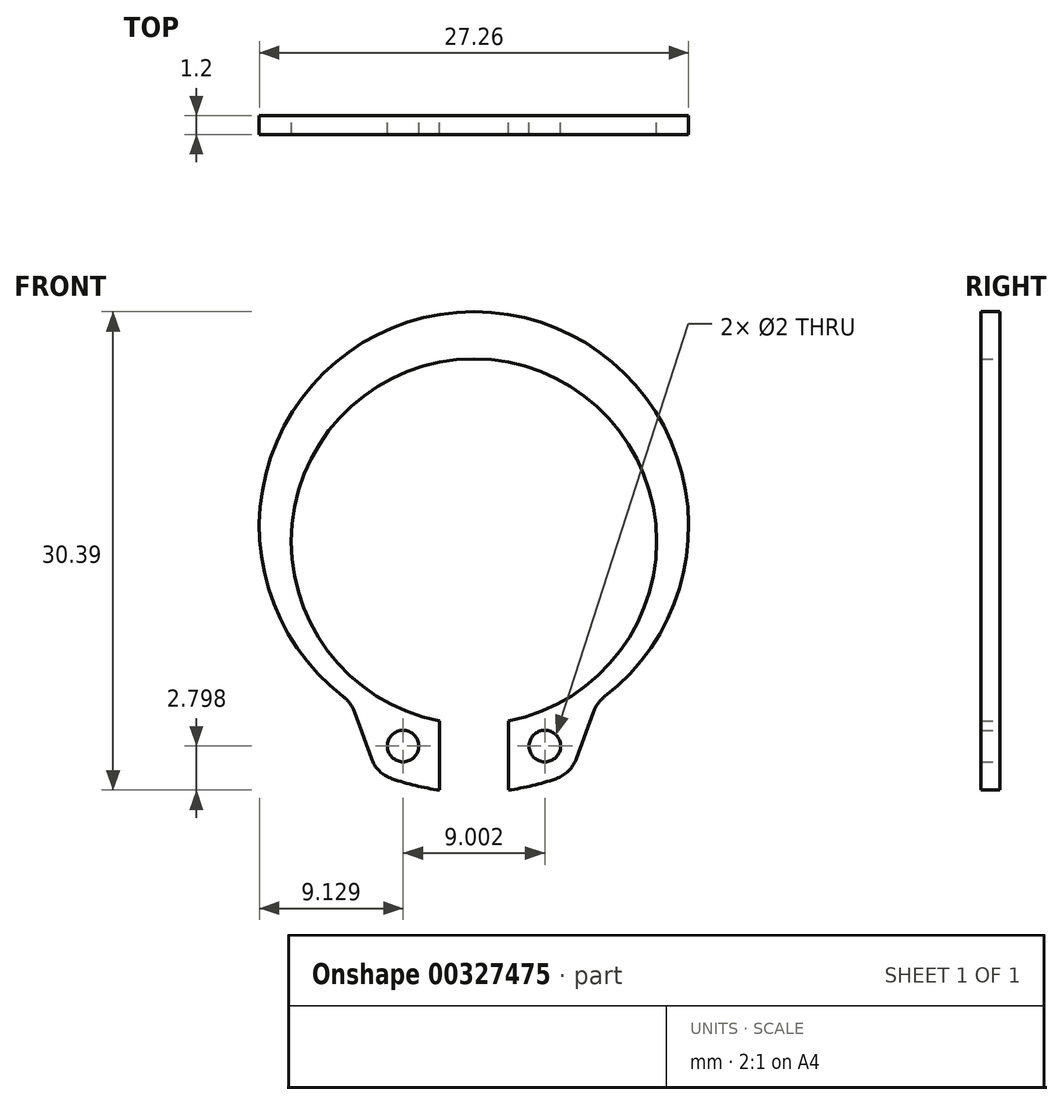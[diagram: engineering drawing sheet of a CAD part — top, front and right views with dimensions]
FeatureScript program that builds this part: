
annotation { "Feature Type Name" : "Feature", "Feature Type Description" : "" }
export const myFeature = defineFeature(function(context is Context, id is Id, definition is map)
    precondition{}
    {
        {
            var Q0;
            Q0=qCreatedBy(makeId("Front.planeOp"),FACE);
            var sketch = newSketch(context, id + "F0", { "sketchPlane" : qUnion([Q0])});
            skCircle(sketch, "E0", {"center": v(0, 0) * mm, "radius": 17.1 * mm, "construction": true});
            skArc(sketch, "E1", {"start": v(2.2, -11.39) * mm, "mid": v(0, 11.6) * mm, "end": v(-2.2, -11.39) * mm});
            skLineSegment(sketch, "E2", {"start": v(2.2, -11.39) * mm, "end": v(2.2, -15.79) * mm});
            skLineSegment(sketch, "E3", {"start": v(0, 0) * mm, "end": v(0, 16.86) * mm, "construction": true});
            skLineSegment(sketch, "E4", {"start": v(-2.2, -11.39) * mm, "end": v(-2.2, -15.79) * mm});
            skLineSegment(sketch, "E5", {"start": v(-2.2, -11.39) * mm, "end": v(0, -11.39) * mm, "construction": true});
            skCircle(sketch, "E6", {"center": v(-4.5, -13) * mm, "radius": 1 * mm});
            skCircle(sketch, "E7", {"center": v(4.5, -13) * mm, "radius": 1 * mm});
            skPoint(sketch, "E8", {"position": v(-2.2, -12.49) * mm});
            skArc(sketch, "E9", {"start": v(2.2, -12.49) * mm, "mid": v(0, 14.6) * mm, "end": v(-2.2, -12.49) * mm});
            skLineSegment(sketch, "E10", {"start": v(0, -11.39) * mm, "end": v(2.2, -11.39) * mm, "construction": true});
            skLineSegment(sketch, "E11", {"start": v(0, 0) * mm, "end": v(-11.6, 0) * mm, "construction": true});
            skLineSegment(sketch, "E12", {"start": v(0, 0) * mm, "end": v(11.6, 0) * mm, "construction": true});
            skLineSegment(sketch, "E13", {"start": v(11.6, 0) * mm, "end": v(13.6, 0) * mm, "construction": true});
            skLineSegment(sketch, "E14", {"start": v(-11.6, 0) * mm, "end": v(-13.6, 0) * mm, "construction": true});
            skArc(sketch, "E15", {"start": v(2.2, -15.79) * mm, "mid": v(4.23, -15.37) * mm, "end": v(6.18, -14.7) * mm});
            skLineSegment(sketch, "E16", {"start": v(-4.5, -13) * mm, "end": v(-4.5, -10.7) * mm, "construction": true});
            skLineSegment(sketch, "E17", {"start": v(-4.5, -13) * mm, "end": v(-4.5, -15.3) * mm, "construction": true});
            skLineSegment(sketch, "E18", {"start": v(4.5, -13) * mm, "end": v(4.5, -10.7) * mm, "construction": true});
            skLineSegment(sketch, "E19", {"start": v(4.5, -13) * mm, "end": v(4.5, -15.3) * mm, "construction": true});
            skLineSegment(sketch, "E20", {"start": v(-4.5, -13) * mm, "end": v(-2.2, -13) * mm, "construction": true});
            skLineSegment(sketch, "E21", {"start": v(4.5, -13) * mm, "end": v(2.2, -13) * mm, "construction": true});
            skLineSegment(sketch, "E22", {"start": v(-6.18, -14.7) * mm, "end": v(-7.82, -10.2) * mm});
            skLineSegment(sketch, "E23.MirrorCS", {"start": v(6.18, -14.7) * mm, "end": v(7.82, -10.2) * mm});
            skLineSegment(sketch, "E24", {"start": v(-4.5, -13) * mm, "end": v(-6.8, -13) * mm, "construction": true});
            skArc(sketch, "E25.trimOffspring", {"start": v(-6.18, -14.7) * mm, "mid": v(-4.23, -15.37) * mm, "end": v(-2.2, -15.79) * mm});
            skCircle(sketch, "E26", {"center": v(0, 0) * mm, "radius": 12.5 * mm, "construction": true});
            skSolve(sketch);
        }
        {
            var Q0;
            Q0=qSketchRegion(id+"F0",true);
            extrude(context, id + "F1", {"entities" : qUnion([Q0]), "depth" : 1.2 * mm});
        }
        {
            var Q0;
            Q0=makeQuery(id+"F1.opExtrude","SWEPT_EDGE",EDGE,{"disambiguationData":[OSD([sQuery(id+"F0.wireOp",EDGE,"907c1e65-be0d-4d4d-923e-d7fc0afcae600.MirrorCS"),sQuery(id+"F0.wireOp",EDGE,"ea3ce9a1-426e-48f8-a769-742e162fd32d0.MirrorCS")])]});
            var Q1;
            Q1=makeQuery(id+"F1.opExtrude","SWEPT_EDGE",EDGE,{"disambiguationData":[OSD([sQuery(id+"F0.wireOp",EDGE,"yB3Dk9i2-sZMU-oLhI-pwqJ-xhCv1nncbOm0"),sQuery(id+"F0.wireOp",EDGE,"pRWJiajO-2Cuv-CeR1-zJug-2Vsa7C0coXul")])]});
            var Q2;
            Q2=makeQuery(id+"F1.opExtrude","SWEPT_EDGE",EDGE,{"disambiguationData":[OSD([sQuery(id+"F0.wireOp",EDGE,"E15"),sQuery(id+"F0.wireOp",EDGE,"E23.MirrorCS")])]});
            var Q3;
            Q3=makeQuery(id+"F1.opExtrude","SWEPT_EDGE",EDGE,{"disambiguationData":[OSD([sQuery(id+"F0.wireOp",EDGE,"E22"),sQuery(id+"F0.wireOp",EDGE,"E25.trimOffspring")])]});
            var Q4;
            Q4=makeQuery(id+"F1.opExtrude","SWEPT_EDGE",EDGE,{"disambiguationData":[OSD([sQuery(id+"F0.wireOp",EDGE,"E9"),sQuery(id+"F0.wireOp",EDGE,"E22")])]});
            var Q5;
            Q5=makeQuery(id+"F1.opExtrude","SWEPT_EDGE",EDGE,{"disambiguationData":[OSD([sQuery(id+"F0.wireOp",EDGE,"E9"),sQuery(id+"F0.wireOp",EDGE,"E23.MirrorCS")])]});
            fillet(context, id + "F2", {"entities" : qUnion([Q0, Q1, Q2, Q3, Q4, Q5]), "radius" : 2.15 * mm, "tangentPropagation" : true, "allowEdgeOverflow" : false});
        }
    });
